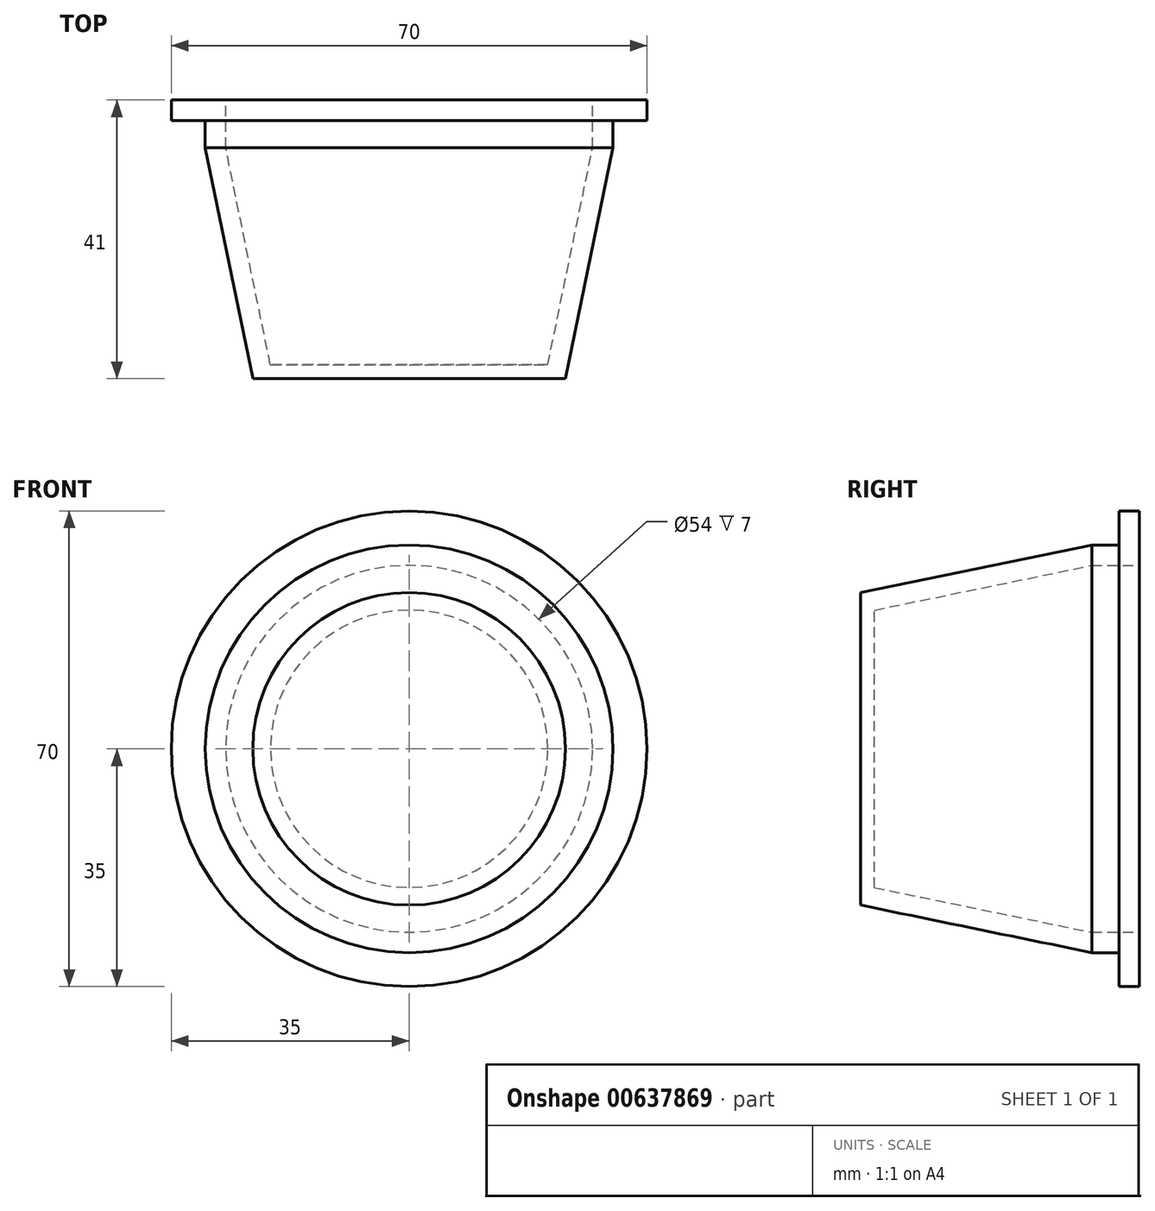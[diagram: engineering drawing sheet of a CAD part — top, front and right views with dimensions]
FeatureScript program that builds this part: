
annotation { "Feature Type Name" : "Feature", "Feature Type Description" : "" }
export const myFeature = defineFeature(function(context is Context, id is Id, definition is map)
    precondition{}
    {
        {
            var Q0;
            Q0=qCreatedBy(makeId("Front.planeOp"),FACE);
            var sketch = newSketch(context, id + "F0", { "sketchPlane" : qUnion([Q0])});
            skCircle(sketch, "E0", {"center": v(0, 0) * mm, "radius": 30 * mm});
            skCircle(sketch, "E1", {"center": v(0, 0) * mm, "radius": 27 * mm});
            skSolve(sketch);
        }
        {
            var Q0;
            Q0=qSketchRegion(id+"F0",true);
            extrude(context, id + "F1", {"entities" : qUnion([Q0]), "depth" : 4 * mm, "offsetDistance" : 25 * mm});
        }
        {
            var Q0;
            Q0=qCreatedBy(makeId("Front.planeOp"),FACE);
            cPlane(context, id + "F2", {"entities" : qUnion([Q0]), "cplaneType" : CPlaneType.OFFSET, "offset" : 38 * mm, "width" : 150 * mm, "height" : 150 * mm});
        }
        {
            var Q0;
            Q0=qCreatedBy(id+"F2.planeOp",FACE);
            var sketch = newSketch(context, id + "F3", { "sketchPlane" : qUnion([Q0])});
            skCircle(sketch, "E2", {"center": v(0, 0) * mm, "radius": 23 * mm});
            skCircle(sketch, "E3", {"center": v(0, 0) * mm, "radius": 20 * mm, "construction": true});
            skSolve(sketch);
        }
        {
            var Q0;
            Q0=makeQuery(id+"F1.opExtrude","CAP_FACE",FACE,{"disambiguationData":[OSD([sQuery(id+"F0.wireOp",EDGE,"E0"),sQuery(id+"F0.wireOp",EDGE,"E1")])],"isStart":false});
            var sketch = newSketch(context, id + "F4", { "sketchPlane" : qUnion([Q0])});
            skCircle(sketch, "E4", {"center": v(0, 0) * mm, "radius": 30 * mm});
            skCircle(sketch, "E5", {"center": v(0, 0) * mm, "radius": 27 * mm, "construction": true});
            skSolve(sketch);
        }
        {
            var Q1;
            Q1=qSketchRegion(id+"F4",true);
            var Q2;
            Q2=qSketchRegion(id+"F3",true);
            loft(context, id + "F5", {"operationType" : NewBodyOperationType.ADD, "sheetProfilesArray" : [{ "sheetProfileEntities" : qUnion([Q1]) }, { "sheetProfileEntities" : qUnion([Q2]) }]});
        }
        {
            var Q0;
            Q0=makeQuery(id+"F5.opLoft","CAP_FACE",FACE,{"disambiguationData":[OSD([makeQuery(id+"F4.imprint","IMPRINT",FACE,{"disambiguationData":[TD([[makeQuery(id+"F4.imprint","IMPRINT",EDGE,{"derivedFrom":makeQuery(id+"F1.opExtrude","CAP_EDGE",EDGE,{"disambiguationData":[OSD([sQuery(id+"F0.wireOp",EDGE,"E1")])],"isStart":false})}),1.0]])]})])],"isStart":true});
            var sketch = newSketch(context, id + "F6", { "sketchPlane" : qUnion([Q0])});
            skCircle(sketch, "E6", {"center": v(0, 0) * mm, "radius": 27 * mm});
            skSolve(sketch);
        }
        {
            var Q0;
            Q0=makeQuery(id+"F5.opLoft","CAP_FACE",FACE,{"disambiguationData":[OSD([makeQuery(id+"F3.imprint","IMPRINT",FACE,{"disambiguationData":[TD([[makeQuery(id+"F3.imprint","IMPRINT",EDGE,{"derivedFrom":sQuery(id+"F3.wireOp",EDGE,"E2")}),1.0]])]})])],"isStart":true});
            var sketch = newSketch(context, id + "F7", { "sketchPlane" : qUnion([Q0])});
            skCircle(sketch, "E7", {"center": v(0, 0) * mm, "radius": 20 * mm});
            skSolve(sketch);
        }
        {
            var Q1;
            Q1=qSketchRegion(id+"F7",true);
            var Q2;
            Q2=qSketchRegion(id+"F6",true);
            loft(context, id + "F8", {"operationType" : NewBodyOperationType.REMOVE, "sheetProfilesArray" : [{ "sheetProfileEntities" : qUnion([Q1]) }, { "sheetProfileEntities" : qUnion([Q2]) }]});
        }
        {
            var Q0;
            Q0=makeQuery(id+"F5.opLoft","CAP_FACE",FACE,{"disambiguationData":[OSD([makeQuery(id+"F3.imprint","IMPRINT",FACE,{"disambiguationData":[TD([[makeQuery(id+"F3.imprint","IMPRINT",EDGE,{"derivedFrom":sQuery(id+"F3.wireOp",EDGE,"E2")}),1.0]])]})])],"isStart":true});
            var sketch = newSketch(context, id + "F9", { "sketchPlane" : qUnion([Q0])});
            skCircle(sketch, "E8", {"center": v(0, 0) * mm, "radius": 22.4 * mm});
            skCircle(sketch, "E9", {"center": v(0, 0) * mm, "radius": 12.7 * mm});
            skSolve(sketch);
        }
        {
            var Q0;
            Q0=qSketchRegion(id+"F9",true);
            extrude(context, id + "F10", {"entities" : qUnion([Q0]), "operationType" : NewBodyOperationType.ADD, "oppositeDirection" : true, "depth" : 2 * mm, "offsetDistance" : 25 * mm});
        }
        {
            var Q0;
            Q0=makeQuery(id+"F1.opExtrude","CAP_FACE",FACE,{"disambiguationData":[OSD([sQuery(id+"F0.wireOp",EDGE,"E0"),sQuery(id+"F0.wireOp",EDGE,"E1")])],"isStart":true});
            var sketch = newSketch(context, id + "F11", { "sketchPlane" : qUnion([Q0])});
            skCircle(sketch, "E10", {"center": v(0, 0) * mm, "radius": 27 * mm});
            skCircle(sketch, "E11", {"center": v(0, 0) * mm, "radius": 35 * mm});
            skSolve(sketch);
        }
        {
            var Q0;
            Q0 = qSketchRegion(id + "F11", true);
            extrude(context, id + "F12", {"entities" : qUnion([Q0]), "operationType" : NewBodyOperationType.ADD, "depth" : 3 * mm, "offsetDistance" : 25 * mm});
        }
        {
            var Q0;
            Q0=makeQuery(id+"F10.boolean.opBoolean","MERGE",FACE,{"derivedFrom":[makeQuery(id+"F5.opLoft","CAP_FACE",FACE,{"disambiguationData":[OSD([makeQuery(id+"F3.imprint","IMPRINT",FACE,{"disambiguationData":[TD([[makeQuery(id+"F3.imprint","IMPRINT",EDGE,{"derivedFrom":sQuery(id+"F3.wireOp",EDGE,"E2")}),1.0]])]})])],"isStart":true}),makeQuery(id+"F10.opExtrude","CAP_FACE",FACE,{"disambiguationData":[OSD([sQuery(id+"F9.wireOp",EDGE,"E8"),sQuery(id+"F9.wireOp",EDGE,"E9")])],"isStart":true})]});
            var sketch = newSketch(context, id + "F13", { "sketchPlane" : qUnion([Q0])});
            skCircle(sketch, "E12", {"center": v(0, 0) * mm, "radius": 16.74 * mm});
            skSolve(sketch);
        }
        {
            var Q0;
            Q0 = qSketchRegion(id + "F13", true);
            extrude(context, id + "F14", {"entities" : qUnion([Q0]), "operationType" : NewBodyOperationType.ADD, "oppositeDirection" : true, "depth" : 2 * mm, "offsetDistance" : 25 * mm});
        }
    });
